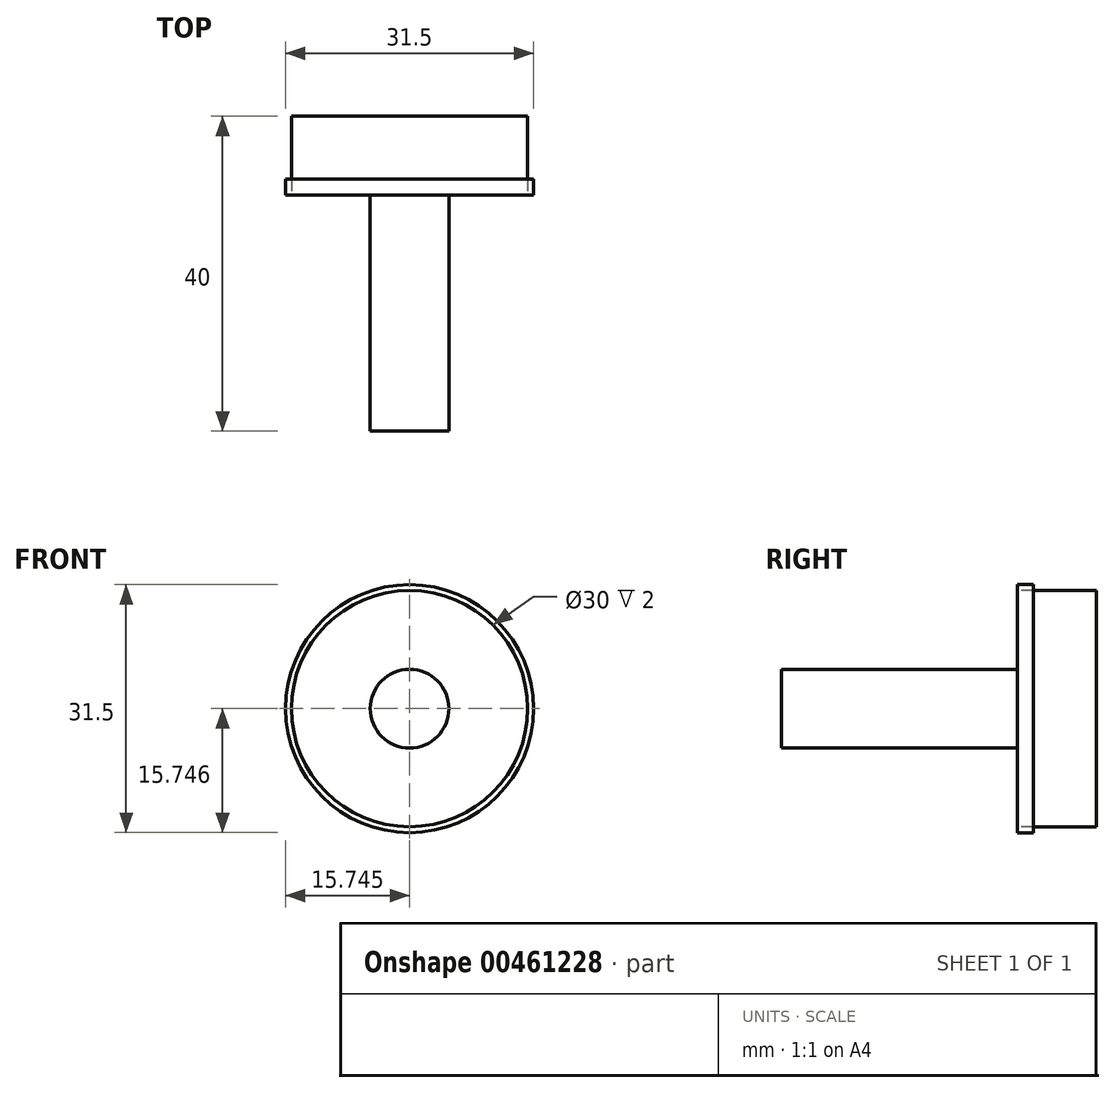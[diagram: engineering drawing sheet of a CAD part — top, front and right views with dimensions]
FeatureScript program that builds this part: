
annotation { "Feature Type Name" : "Feature", "Feature Type Description" : "" }
export const myFeature = defineFeature(function(context is Context, id is Id, definition is map)
    precondition{}
    {
        {
            var Q0;
            Q0=qCreatedBy(makeId("Front.planeOp"),FACE);
            var sketch = newSketch(context, id + "F0", { "sketchPlane" : qUnion([Q0])});
            skCircle(sketch, "E0", {"center": v(-39.21, 34.09) * mm, "radius": 15 * mm});
            skCircle(sketch, "E1", {"center": v(-39.21, 34.09) * mm, "radius": 5 * mm});
            skCircle(sketch, "E2", {"center": v(-39.21, 34.09) * mm, "radius": 16 * mm});
            skSolve(sketch);
        }
        {
            var Q0;
            Q0=makeQuery(id+"F0.imprint","IMPRINT",FACE,{"disambiguationData":[TD([[makeQuery(id+"F0.imprint","IMPRINT",EDGE,{"derivedFrom":sQuery(id+"F0.wireOp",EDGE,"E0")}),1.0]])]});
            extrude(context, id + "F1", {"entities" : qUnion([Q0]), "depth" : 10 * mm});
        }
        {
            var Q0;
            Q0=makeQuery(id+"F0.imprint","IMPRINT",FACE,{"disambiguationData":[TD([[makeQuery(id+"F0.imprint","IMPRINT",EDGE,{"derivedFrom":sQuery(id+"F0.wireOp",EDGE,"E1")}),1.0]])]});
            extrude(context, id + "F2", {"entities" : qUnion([Q0]), "operationType" : NewBodyOperationType.ADD, "depth" : 40 * mm});
        }
        {
            var Q0;
            Q0=qCreatedBy(makeId("Front.planeOp"),FACE);
            cPlane(context, id + "F3", {"entities" : qUnion([Q0]), "cplaneType" : CPlaneType.OFFSET, "offset" : 10 * mm, "width" : 150 * mm, "height" : 150 * mm});
        }
        {
            var Q0;
            Q0=makeQuery(id+"F1.opExtrude","CAP_FACE",FACE,{"disambiguationData":[OSD([sQuery(id+"F0.wireOp",EDGE,"E0"),sQuery(id+"F0.wireOp",EDGE,"E1")])],"isStart":false});
            var sketch = newSketch(context, id + "F4", { "sketchPlane" : qUnion([Q0])});
            skCircle(sketch, "E3", {"center": v(-39.21, 34.09) * mm, "radius": 15.75 * mm});
            skSolve(sketch);
        }
        {
            var Q0;
            Q0=makeQuery(id+"F4.imprint","IMPRINT",FACE,{"disambiguationData":[TD([[makeQuery(id+"F4.imprint","IMPRINT",EDGE,{"derivedFrom":sQuery(id+"F4.wireOp",EDGE,"E3")}),1.0]])]});
            extrude(context, id + "F5", {"entities" : qUnion([Q0]), "oppositeDirection" : true, "depth" : 2 * mm});
        }
    });
